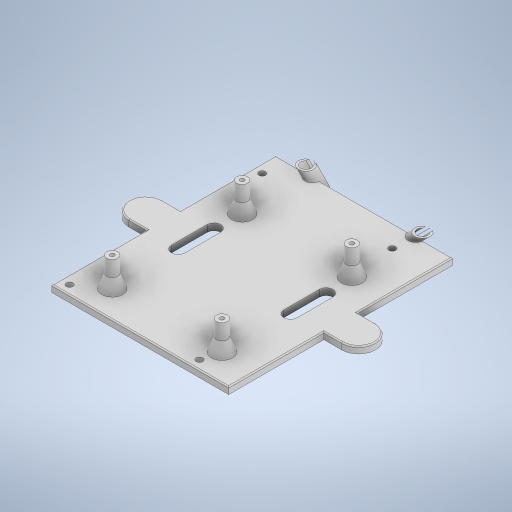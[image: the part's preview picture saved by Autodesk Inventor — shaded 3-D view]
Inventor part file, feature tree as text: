
AUTODESK INVENTOR PART (.ipt)
format: ipt  version: 2023.2 (Build 272271030, 271C)  size: 433,152 bytes
history: native  units: mm
features: sketch x4, chamfer x4, sweep x4, extrude x3, plane x1, mirror x1, fillet x1
ambient origin geometry x8: Origin, YZ Plane, XZ Plane, XY Plane, X Axis, Y Axis, Z Axis, Center Point
bodies: Solid1 (feature_tree)
feature tree (18):
  sketch  "Sketch1"  dims[d12=100.0mm d13=4.0mm d14=3.0mm d15=4.0mm d16=3.0mm d17=58.0mm d18=3.0mm d19=86.0mm d20=86.0mm d21=58.0mm d22=17.0mm d23=4.0mm d24=3.0mm d25=50.0mm d27=79.0mm d44=39.5mm]
  extrude  "Extrusion1"  Depth=39.5mm
  extrude  "Extrusion2"  Depth=5.0mm
  extrude  "Extrusion3"  Depth=49.0mm
  chamfer  "Chamfer1"  Distance=30.0mm
  sketch  "Sketch3"  dims[d48=5.0mm d51=49.0mm]
  sweep  "Sweep1"
  sweep  "Sweep2"
  sweep  "Sweep3"
  plane  "Work Plane1"
  mirror  "Mirror4"
  sweep  "Sweep4"
  chamfer  "Chamfer2"  Distance=2.0mm
  chamfer  "Chamfer3"  Distance=5.0mm
  chamfer  "Chamfer4"  Distance=2.0mm
  fillet  "Fillet1"  Radius=2.0mm
  sketch  "Sketch2"  dims[d45=50.0mm d47=5.0mm]
  sketch  "Sketch4"  dims[d53=49.0mm d54=30.0mm d55=58.0mm d64=3.0mm d65=0.0mm d66=16.0mm d67=0.0mm d68=5.0mm d69=2.0mm d70=5.0mm d71=0.0mm d72=2.0mm d73=2.0mm d74=2.0mm d75=6.0mm d76=2.0mm d77=3.490659mm d85=6.8mm d86=4.8mm d87=6.8mm d88=4.8mm d89=20.0mm d90=20.0mm d92=135.0deg d93=6.0mm d94=0.0mm d95=0.0mm d96=0.0mm d97=0.0mm d98=2.0mm d99=2.0mm d100=0.0mm d101=0.0mm d102=-39.5mm d103=45.0deg d104=6.0mm d105=0.0mm d106=0.0mm d107=6.0mm d108=2.0mm d109=3.490659mm d110=6.0mm d111=2.0mm d112=3.490659mm d113=6.0mm d114=2.0mm d115=3.490659mm d116=0.5mm d118=8.0mm d119=15.0mm]
